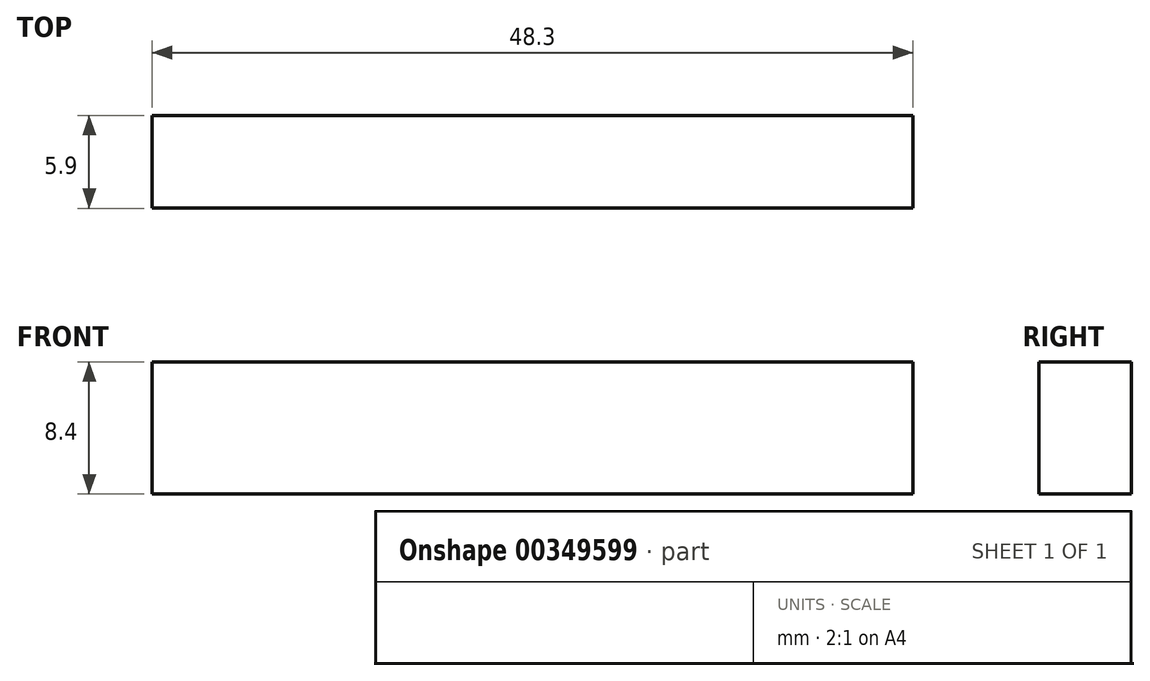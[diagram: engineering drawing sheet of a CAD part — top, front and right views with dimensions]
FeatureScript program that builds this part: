
annotation { "Feature Type Name" : "Feature", "Feature Type Description" : "" }
export const myFeature = defineFeature(function(context is Context, id is Id, definition is map)
    precondition{}
    {
        {
            var Q0;
            Q0=qCreatedBy(makeId("Top.planeOp"),FACE);
            var sketch = newSketch(context, id + "F0", { "sketchPlane" : qUnion([Q0])});
            skLineSegment(sketch, "E0.bottom", {"start": v(-48.3, -4) * mm, "end": v(0, -4) * mm});
            skLineSegment(sketch, "E0.top", {"start": v(-48.3, 1.9) * mm, "end": v(0, 1.9) * mm});
            skLineSegment(sketch, "E0.left", {"start": v(-48.3, -4) * mm, "end": v(-48.3, 1.9) * mm});
            skLineSegment(sketch, "E0.right", {"start": v(0, -4) * mm, "end": v(0, 1.9) * mm});
            skSolve(sketch);
        }
        {
            var Q0;
            Q0=makeQuery(id+"F0.imprint","IMPRINT",FACE,{"disambiguationData":[TD([[makeQuery(id+"F0.imprint","IMPRINT",EDGE,{"derivedFrom":sQuery(id+"F0.wireOp",EDGE,"E0.bottom")}),1.0]])]});
            extrude(context, id + "F1", {"entities" : qUnion([Q0]), "depth" : 8.4 * mm, "offsetDistance" : 25.4 * mm});
        }
    });
